# Revit family: Deca_Porta toalha barra 30cm_Clean_2040.030.CLN
name_source: partatom
category: Plumbing Fixtures
units: mm (PartAtom-declared; Revit-internal decimal feet)

## family parameters
Cut with Voids When Loaded = No
Host = Face
Part Type = Normal
Room Calculation Point = No
Round Connector Dimension = Use Diameter
Shared = No

## types (3) — shared parameters
Acompanha o Produto = Acompanha Parafusos e Buchas para fixação para alvenaria
Aprovado por = quattroD
Atendimento ao Cliente = 0800-0117073
Categoria = ACESSORIOS
Composição Anel Vedação = -
Composição Assento = -
Composição Básica = Liga de Cobre (bronze e latão),Plásticos de Engenharia
Composição Componente = -
Consumo = -
Cor Interna = -
Cor Secundária = -
Cores Componente = -
Criado por = quattroD
Código Pai = 2040.030.CLN
Default Elevation = 1100 mm
Description = Porta toalha barra 30cm
Informações Complementares = -
Itens de Instalação = -
Linha = Acessório Clean
Manufacturer = Deca
Norma = Não Possui
Pressão máx. funcionamento = -
Pressão mín. Aquec. Acúmulo = -
Pressão mín. Aquec. Passagem = -
Pressão mín. funcionamento = -
Saída de Esgoto = -
Segmento = Banheiro Médio
Tipo de dispositivo economizador = -
Tipo de mecanismo utilizado = -
Tipo de rosca de entrada = -
Tipo de rosca de saída = -
URL = www.deca.com.br
Vazão na Pressão máx. (L/min) = -
Vazão na Pressão mín. (L/min) = -
zero-valued in all types: HWFU

## per-type parameters (varying)
| type | Cor Principal | Material | Model | Peso Líquido (Kg) |
| 2040.C.030.CLN_Cromado | Cromado | Deca_Cromado | 2040.C.030.CLN | 0.449 |
| 2040.BL.030.CLN.NO_Black Noir | Black Noir | Deca_Black Noir | 2040.BL.030.CLN.NO | 0.441 |
| 2040.GL.030.CLN.RD_Red Gold | Red Gold | Deca_Red Gold | 2040.GL.030.CLN.RD | 0.449 |
